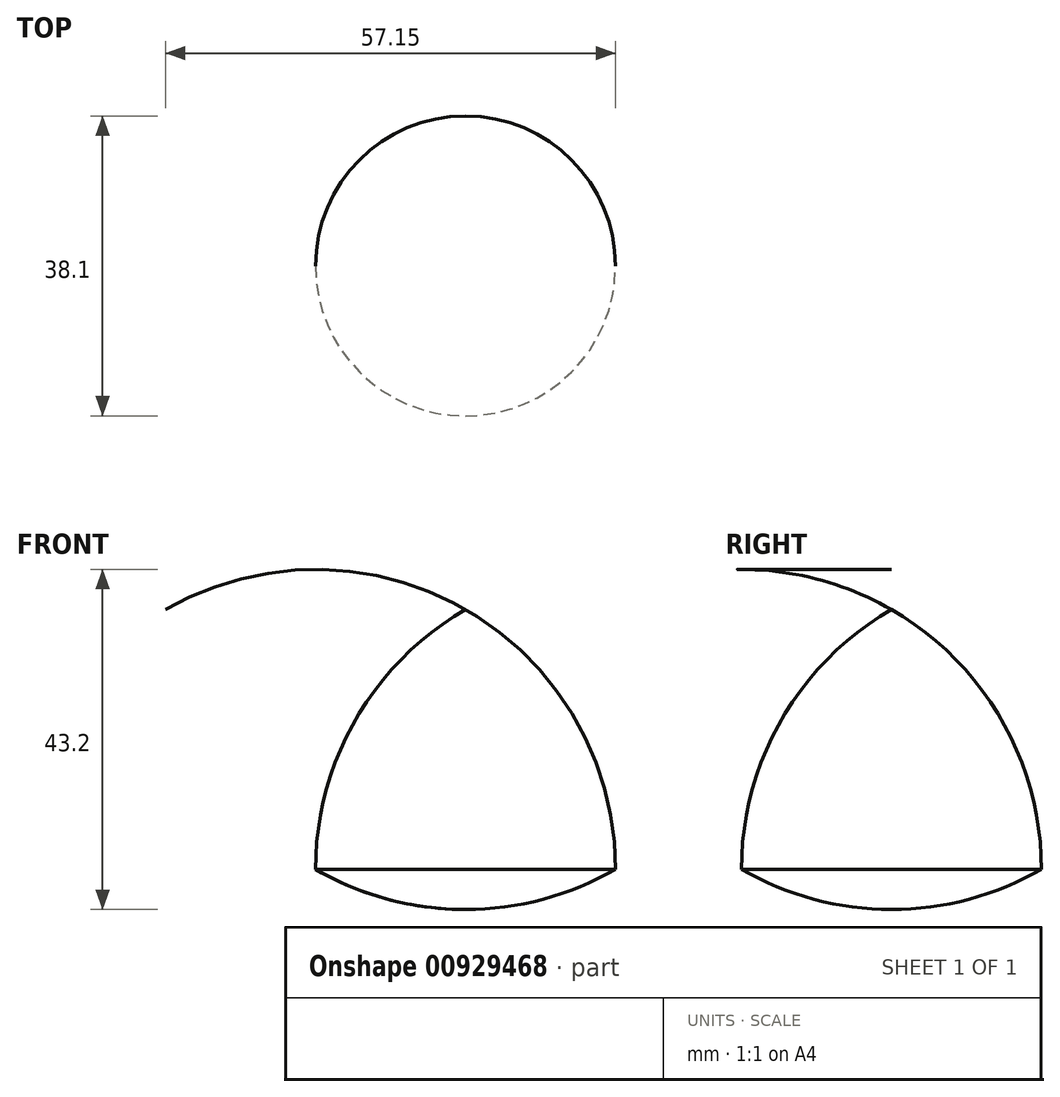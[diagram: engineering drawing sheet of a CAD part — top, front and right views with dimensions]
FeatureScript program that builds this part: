
annotation { "Feature Type Name" : "Feature", "Feature Type Description" : "" }
export const myFeature = defineFeature(function(context is Context, id is Id, definition is map)
    precondition{}
    {
        {
            var Q0;
            Q0=qCreatedBy(makeId("Front.planeOp"),FACE);
            var sketch = newSketch(context, id + "F0", { "sketchPlane" : qUnion([Q0])});
            skPoint(sketch, "E0", {"position": v(-52.7, 36.76) * mm});
            skPoint(sketch, "E1.center.orphan", {"position": v(-52.7, 3.76) * mm});
            skArc(sketch, "E2", {"start": v(-71.75, 36.76) * mm, "mid": v(-52.7, 31.66) * mm, "end": v(-33.65, 36.76) * mm});
            skArc(sketch, "E3", {"start": v(-33.65, 36.76) * mm, "mid": v(-38.76, 55.81) * mm, "end": v(-52.7, 69.76) * mm});
            skArc(sketch, "E4.trimOffspring", {"start": v(-52.7, 69.76) * mm, "mid": v(-66.65, 55.81) * mm, "end": v(-71.75, 36.76) * mm});
            skLineSegment(sketch, "E5", {"start": v(-52.7, 69.76) * mm, "end": v(-52.7, 31.66) * mm});
            skSolve(sketch);
        }
        {
            var Q0;
            Q0=makeQuery(id+"F0.imprint","IMPRINT",FACE,{"disambiguationData":[TD([[makeQuery(id+"F0.imprint","IMPRINT",EDGE,{"derivedFrom":sQuery(id+"F0.wireOp",EDGE,"E2")}),1.0]])]});
            var Q1;
            Q1=sQuery(id+"F0.wireOp",EDGE,"E4.trimOffspring");
            var Q2;
            Q2=sQuery(id+"F0.wireOp",EDGE,"E5");
            revolve(context, id + "F1", {"bodyType" : ToolBodyType.SURFACE, "operationType" : NewBodyOperationType.ADD, "surfaceOperationType" : NewSurfaceOperationType.NEW, "entities" : qUnion([Q0]), "surfaceEntities" : qUnion([Q1]), "axis" : qUnion([Q2]), "revolveType" : RevolveType.ONE_DIRECTION, "oppositeDirection" : true, "angle" : 360 * degree});
        }
        {
            var Q0;
            {var subQ0=sQuery(id+"F0.wireOp",EDGE,"E4.trimOffspring");Q0=makeQuery(id+"F0.imprint","IMPRINT",FACE,{"disambiguationData":[TD([[makeQuery(id+"F0.imprint","IMPRINT",EDGE,{"derivedFrom":subQ0}),1.0]])]});}
            var Q1;
            Q1=sQuery(id+"F0.wireOp",EDGE,"E2");
            var Q2;
            Q2=makeQuery(id+"F1.opRevolve","SWEPT_FACE",FACE,{"disambiguationData":[OSD([sQuery(id+"F0.wireOp",EDGE,"E4.trimOffspring")])]});
            revolve(context, id + "F2", {"surfaceOperationType" : NewSurfaceOperationType.ADD, "entities" : qUnion([Q0]), "surfaceEntities" : qUnion([Q1]), "axis" : qUnion([Q2]), "revolveType" : RevolveType.FULL});
        }
    });
